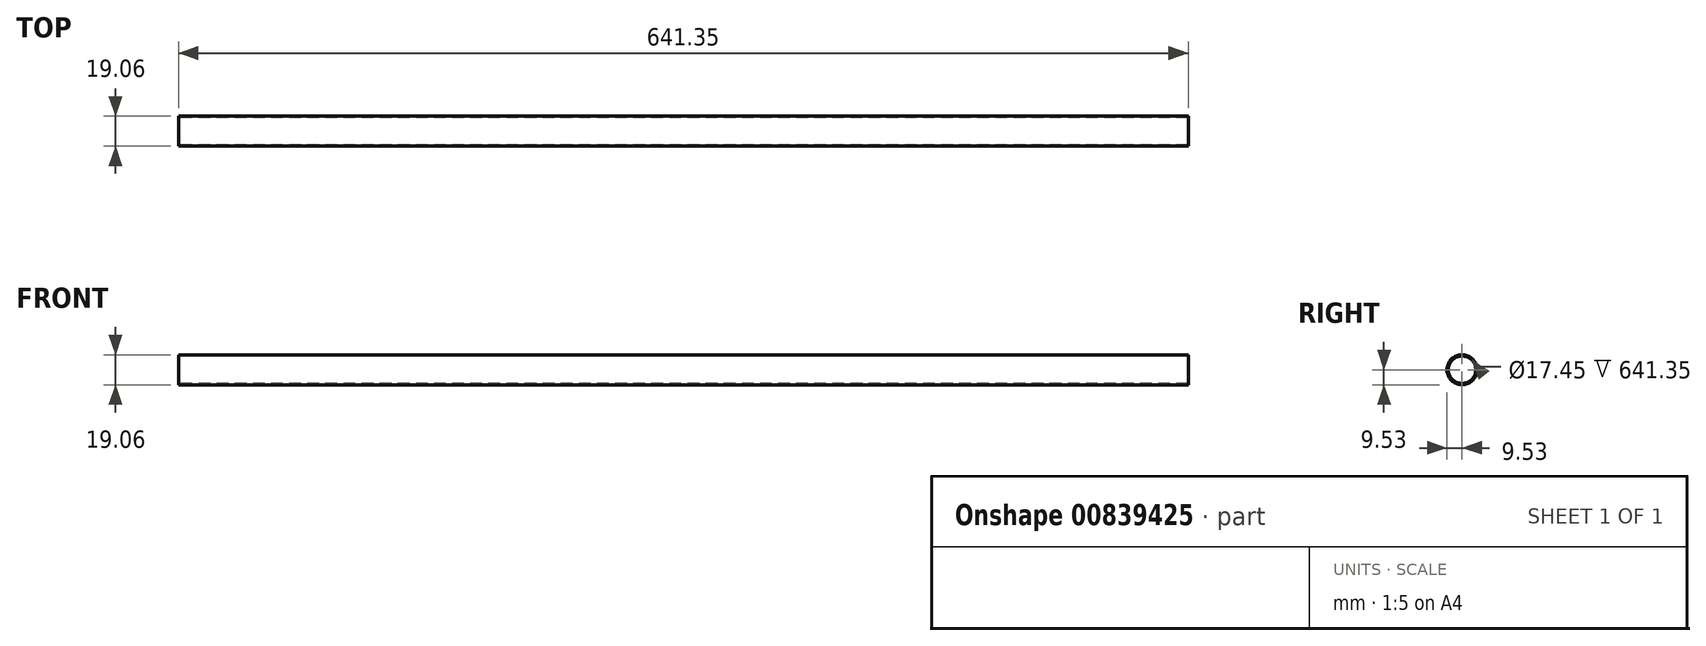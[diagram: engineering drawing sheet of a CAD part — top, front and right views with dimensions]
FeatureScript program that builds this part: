
annotation { "Feature Type Name" : "Feature", "Feature Type Description" : "" }
export const myFeature = defineFeature(function(context is Context, id is Id, definition is map)
    precondition{}
    {
        {
            var Q0;
            Q0=qCreatedBy(makeId("Right.planeOp"),FACE);
            var sketch = newSketch(context, id + "F0", { "sketchPlane" : qUnion([Q0])});
            skCircle(sketch, "E0", {"center": v(0, 0) * mm, "radius": 9.53 * mm});
            skCircle(sketch, "E1", {"center": v(0, 0) * mm, "radius": 8.72 * mm});
            skSolve(sketch);
        }
        {
            var Q0;
            Q0 = qSketchRegion(id + "F0", true);
            extrude(context, id + "F1", {"entities" : qUnion([Q0]), "depth" : 641.35 * mm, "offsetDistance" : 25.4 * mm});
        }
    });
